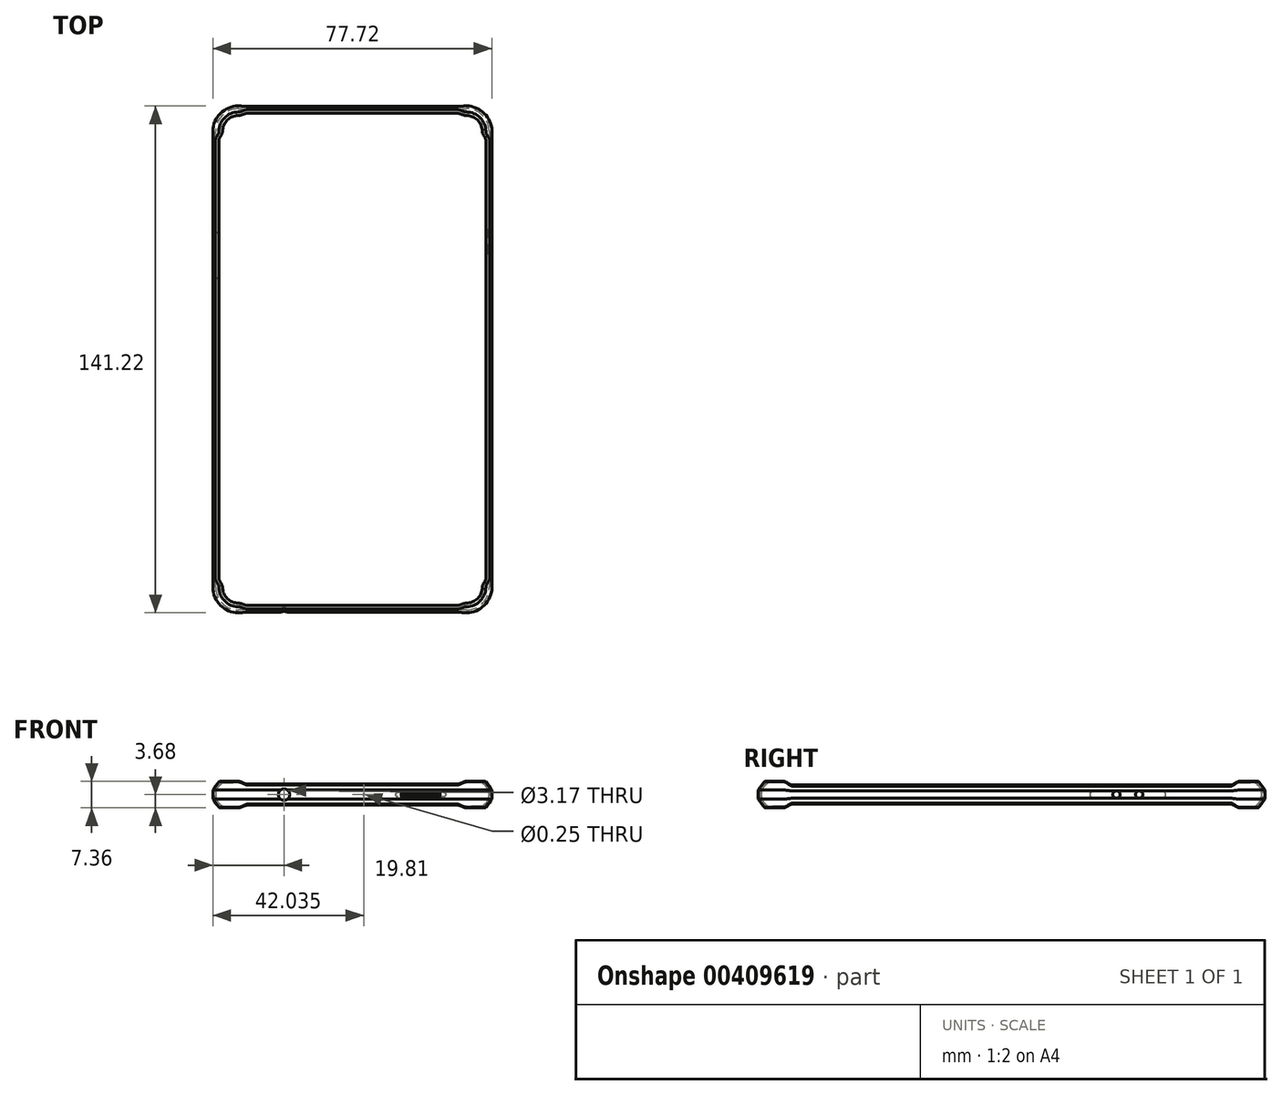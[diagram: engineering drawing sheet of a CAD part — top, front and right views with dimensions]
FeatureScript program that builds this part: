
annotation { "Feature Type Name" : "Feature", "Feature Type Description" : "" }
export const myFeature = defineFeature(function(context is Context, id is Id, definition is map)
    precondition{}
    {
        {
            var Q0;
            Q0=qCreatedBy(makeId("Top.planeOp"),FACE);
            var sketch = newSketch(context, id + "F0", { "sketchPlane" : qUnion([Q0])});
            skLineSegment(sketch, "E0", {"start": v(0, 0) * mm, "end": v(0, -63.5) * mm});
            skLineSegment(sketch, "E1", {"start": v(6.35, -69.85) * mm, "end": v(38.1, -69.85) * mm});
            skPoint(sketch, "E2.visualSharp", {"position": v(0, -69.85) * mm});
            skArc(sketch, "E2.filletArc", {"start": v(0, -63.5) * mm, "mid": v(1.86, -68) * mm, "end": v(6.35, -69.85) * mm});
            skSolve(sketch);
        }
        {
            var Q0;
            Q0=sQuery(id+"F0.wireOp",EDGE,"E1");
            var Q1;
            Q1=sQuery(id+"F0.wireOp",VERTEX,"E1.end");
            cPlane(context, id + "F1", {"entities" : qUnion([Q0, Q1]), "cplaneType" : CPlaneType.LINE_POINT, "offset" : 25.4 * mm, "width" : 152.4 * mm, "height" : 152.4 * mm});
        }
        {
            var Q0;
            Q0=qCreatedBy(id+"F1.planeOp",FACE);
            var sketch = newSketch(context, id + "F2", { "sketchPlane" : qUnion([Q0])});
            skLineSegment(sketch, "E3", {"start": v(-69.68, 0) * mm, "end": v(-65.87, 0) * mm});
            skArc(sketch, "E4", {"start": v(-68.57, 2.7) * mm, "mid": v(-69.68, 0) * mm, "end": v(-68.57, -2.7) * mm});
            skLineSegment(sketch, "E5", {"start": v(-68.57, 2.7) * mm, "end": v(-68.62, 2.75) * mm});
            skLineSegment(sketch, "E6", {"start": v(-68.62, 2.75) * mm, "end": v(-68.57, 2.7) * mm});
            skLineSegment(sketch, "E7", {"start": v(-69.68, 0) * mm, "end": v(-70.44, 0) * mm});
            skLineSegment(sketch, "E8", {"start": v(-70.44, 0) * mm, "end": v(-70.44, 1.27) * mm});
            skLineSegment(sketch, "E9", {"start": v(-70.44, 0) * mm, "end": v(-70.44, -1.27) * mm});
            skLineSegment(sketch, "E10", {"start": v(-68.57, -2.7) * mm, "end": v(-68.62, -2.75) * mm});
            skPoint(sketch, "E11.visualSharp", {"position": v(-69.1, 3.23) * mm});
            skArc(sketch, "E11.filletArc", {"start": v(-68.62, 2.75) * mm, "mid": v(-69.12, 2.93) * mm, "end": v(-69.58, 2.67) * mm});
            skPoint(sketch, "E12.visualSharp", {"position": v(-69.1, -3.23) * mm});
            skArc(sketch, "E12.filletArc", {"start": v(-69.58, -2.67) * mm, "mid": v(-69.12, -2.93) * mm, "end": v(-68.62, -2.75) * mm});
            skLineSegment(sketch, "E13", {"start": v(-70.44, 1.27) * mm, "end": v(-69.58, 2.67) * mm});
            skLineSegment(sketch, "E14", {"start": v(-70.44, -1.27) * mm, "end": v(-69.58, -2.67) * mm});
            skSolve(sketch);
        }
        {
            var Q0;
            Q0 = qSketchRegion(id + "F2", true);
            extrude(context, id + "F3", {"entities" : qUnion([Q0]), "oppositeDirection" : true, "depth" : 29.2 * mm});
        }
        {
            var Q0;
            Q0=qCreatedBy(makeId("Front.planeOp"),FACE);
            var sketch = newSketch(context, id + "F4", { "sketchPlane" : qUnion([Q0])});
            skLineSegment(sketch, "E15", {"start": v(0, 0) * mm, "end": v(3.81, 0) * mm});
            skArc(sketch, "E16", {"start": v(0.9, 2.45) * mm, "mid": v(0, 0) * mm, "end": v(0.9, -2.45) * mm});
            skLineSegment(sketch, "E17", {"start": v(0.9, 2.45) * mm, "end": v(0.83, 2.5) * mm});
            skLineSegment(sketch, "E18", {"start": v(0, 0) * mm, "end": v(-0.76, 0) * mm});
            skLineSegment(sketch, "E19", {"start": v(0.9, -2.45) * mm, "end": v(0.83, -2.5) * mm});
            skLineSegment(sketch, "E20", {"start": v(-0.76, 0) * mm, "end": v(-0.76, 1.02) * mm});
            skLineSegment(sketch, "E21", {"start": v(-0.76, 0) * mm, "end": v(-0.76, -1.02) * mm});
            skPoint(sketch, "E22.visualSharp", {"position": v(0.3, 2.94) * mm});
            skArc(sketch, "E22.filletArc", {"start": v(0.83, 2.5) * mm, "mid": v(0.32, 2.64) * mm, "end": v(-0.12, 2.34) * mm});
            skPoint(sketch, "E23.visualSharp", {"position": v(0.3, -2.94) * mm});
            skArc(sketch, "E23.filletArc", {"start": v(-0.12, -2.34) * mm, "mid": v(0.32, -2.64) * mm, "end": v(0.83, -2.5) * mm});
            skLineSegment(sketch, "E24", {"start": v(-0.76, 1.02) * mm, "end": v(-0.12, 2.34) * mm});
            skLineSegment(sketch, "E25", {"start": v(-0.76, -1.02) * mm, "end": v(-0.12, -2.34) * mm});
            skSolve(sketch);
        }
        {
            var Q0;
            Q0 = qSketchRegion(id + "F4", true);
            extrude(context, id + "F5", {"entities" : qUnion([Q0]), "depth" : 60.96 * mm});
        }
        {
            var Q0;
            Q0=sQuery(id+"F0.wireOp",EDGE,"E0");
            var Q1;
            Q1=sQuery(id+"F0.wireOp",VERTEX,"E2.filletArc.start");
            cPlane(context, id + "F6", {"entities" : qUnion([Q0, Q1]), "cplaneType" : CPlaneType.LINE_POINT, "offset" : 25.4 * mm, "width" : 152.4 * mm, "height" : 152.4 * mm});
        }
        {
            var Q0;
            Q0=qCreatedBy(id+"F6.planeOp",FACE);
            var sketch = newSketch(context, id + "F7", { "sketchPlane" : qUnion([Q0])});
            skLineSegment(sketch, "E26", {"start": v(0, 0) * mm, "end": v(3.8, 0) * mm});
            skArc(sketch, "E27", {"start": v(1.9, 3.3) * mm, "mid": v(0, 0) * mm, "end": v(1.9, -3.3) * mm});
            skLineSegment(sketch, "E28", {"start": v(1.9, 3.3) * mm, "end": v(1.87, 3.36) * mm});
            skLineSegment(sketch, "E29", {"start": v(1.9, -3.3) * mm, "end": v(1.87, -3.36) * mm});
            skLineSegment(sketch, "E30", {"start": v(0, 0) * mm, "end": v(-0.76, 0) * mm});
            skLineSegment(sketch, "E31", {"start": v(-0.76, 0) * mm, "end": v(-0.76, 1.27) * mm});
            skLineSegment(sketch, "E32", {"start": v(-0.76, 0) * mm, "end": v(-0.76, -1.27) * mm});
            skPoint(sketch, "E33.visualSharp", {"position": v(1.52, 3.96) * mm});
            skArc(sketch, "E33.filletArc", {"start": v(1.87, 3.36) * mm, "mid": v(1.43, 3.67) * mm, "end": v(0.92, 3.54) * mm});
            skPoint(sketch, "E34.visualSharp", {"position": v(1.52, -3.96) * mm});
            skArc(sketch, "E34.filletArc", {"start": v(0.92, -3.54) * mm, "mid": v(1.43, -3.67) * mm, "end": v(1.87, -3.36) * mm});
            skLineSegment(sketch, "E35", {"start": v(-0.76, 1.27) * mm, "end": v(0.92, 3.54) * mm});
            skLineSegment(sketch, "E36", {"start": v(-0.76, -1.27) * mm, "end": v(0.92, -3.54) * mm});
            skSolve(sketch);
        }
        {
            var Q0;
            {var subQ1=sQuery(id+"F7.wireOp",EDGE,"E29");Q0=makeQuery(id+"F7.imprint","IMPRINT",FACE,{"disambiguationData":[TD([[makeQuery(id+"F7.imprint","IMPRINT",EDGE,{"derivedFrom":subQ1}),-1.0]])]});}
            var Q1;
            {var subQ1=sQuery(id+"F7.wireOp",EDGE,"E28");Q1=makeQuery(id+"F7.imprint","IMPRINT",FACE,{"disambiguationData":[TD([[makeQuery(id+"F7.imprint","IMPRINT",EDGE,{"derivedFrom":subQ1}),1.0]])]});}
            var Q2;
            Q2=sQuery(id+"F0.wireOp",EDGE,"E2.filletArc");
            sweep(context, id + "F8", {"profiles" : qUnion([Q0, Q1]), "path" : qUnion([Q2])});
        }
        {
            var Q0;
            Q0=makeQuery(id+"F8.opSweep","CAP_FACE",FACE,{"disambiguationData":[OSD([sQuery(id+"F0.wireOp",VERTEX,"E2.filletArc.end"),sQuery(id+"F7.wireOp",EDGE,"E27"),sQuery(id+"F7.wireOp",EDGE,"E28"),sQuery(id+"F7.wireOp",EDGE,"E29"),sQuery(id+"F7.wireOp",EDGE,"E31"),sQuery(id+"F7.wireOp",EDGE,"E32"),sQuery(id+"F7.wireOp",EDGE,"E33.filletArc"),sQuery(id+"F7.wireOp",EDGE,"E34.filletArc"),sQuery(id+"F7.wireOp",EDGE,"E35"),sQuery(id+"F7.wireOp",EDGE,"E36")])],"isStart":false});
            var Q1;
            Q1=makeQuery(id+"F3.opExtrude","CAP_FACE",FACE,{"disambiguationData":[OSD([sQuery(id+"F2.wireOp",EDGE,"E4"),sQuery(id+"F2.wireOp",EDGE,"E6"),sQuery(id+"F2.wireOp",EDGE,"E8"),sQuery(id+"F2.wireOp",EDGE,"E9"),sQuery(id+"F2.wireOp",EDGE,"E10"),sQuery(id+"F2.wireOp",EDGE,"E11.filletArc"),sQuery(id+"F2.wireOp",EDGE,"E12.filletArc"),sQuery(id+"F2.wireOp",EDGE,"E13"),sQuery(id+"F2.wireOp",EDGE,"E14")])],"isStart":false});
            loft(context, id + "F9", {"operationType" : NewBodyOperationType.ADD, "startCondition" : LoftEndDerivativeType.NORMAL_TO_PROFILE, "startMagnitude" : 1, "endCondition" : LoftEndDerivativeType.NORMAL_TO_PROFILE, "endMagnitude" : 1, "sheetProfilesArray" : [{ "sheetProfileEntities" : qUnion([Q0]) }, { "sheetProfileEntities" : qUnion([Q1]) }]});
        }
        {
            var Q0;
            Q0=makeQuery(id+"F5.opExtrude","CAP_FACE",FACE,{"disambiguationData":[OSD([sQuery(id+"F4.wireOp",EDGE,"E16"),sQuery(id+"F4.wireOp",EDGE,"E17"),sQuery(id+"F4.wireOp",EDGE,"E19"),sQuery(id+"F4.wireOp",EDGE,"E20"),sQuery(id+"F4.wireOp",EDGE,"E21"),sQuery(id+"F4.wireOp",EDGE,"E22.filletArc"),sQuery(id+"F4.wireOp",EDGE,"E23.filletArc"),sQuery(id+"F4.wireOp",EDGE,"E24"),sQuery(id+"F4.wireOp",EDGE,"E25")])],"isStart":false});
            var Q1;
            Q1=makeQuery(id+"F8.opSweep","CAP_FACE",FACE,{"disambiguationData":[OSD([sQuery(id+"F0.wireOp",VERTEX,"E2.filletArc.start"),sQuery(id+"F7.wireOp",EDGE,"E27"),sQuery(id+"F7.wireOp",EDGE,"E28"),sQuery(id+"F7.wireOp",EDGE,"E29"),sQuery(id+"F7.wireOp",EDGE,"E31"),sQuery(id+"F7.wireOp",EDGE,"E32"),sQuery(id+"F7.wireOp",EDGE,"E33.filletArc"),sQuery(id+"F7.wireOp",EDGE,"E34.filletArc"),sQuery(id+"F7.wireOp",EDGE,"E35"),sQuery(id+"F7.wireOp",EDGE,"E36")])],"isStart":true});
            loft(context, id + "F10", {"operationType" : NewBodyOperationType.ADD, "startCondition" : LoftEndDerivativeType.NORMAL_TO_PROFILE, "startMagnitude" : 1, "endCondition" : LoftEndDerivativeType.NORMAL_TO_PROFILE, "endMagnitude" : 1, "sheetProfilesArray" : [{ "sheetProfileEntities" : qUnion([Q0]) }, { "sheetProfileEntities" : qUnion([Q1]) }]});
        }
        {
            var Q0;
            Q0=makeQuery(id+"F3.opExtrude","SWEPT_BODY",BODY,{"disambiguationData":[OSD([sQuery(id+"F2.wireOp",EDGE,"E4"),sQuery(id+"F2.wireOp",EDGE,"E6"),sQuery(id+"F2.wireOp",EDGE,"E8"),sQuery(id+"F2.wireOp",EDGE,"E9"),sQuery(id+"F2.wireOp",EDGE,"E10"),sQuery(id+"F2.wireOp",EDGE,"E11.filletArc"),sQuery(id+"F2.wireOp",EDGE,"E12.filletArc"),sQuery(id+"F2.wireOp",EDGE,"E13"),sQuery(id+"F2.wireOp",EDGE,"E14")])]});
            var Q1;
            Q1=makeQuery(id+"F3.opExtrude","CAP_FACE",FACE,{"disambiguationData":[OSD([sQuery(id+"F2.wireOp",EDGE,"E4"),sQuery(id+"F2.wireOp",EDGE,"E6"),sQuery(id+"F2.wireOp",EDGE,"E8"),sQuery(id+"F2.wireOp",EDGE,"E9"),sQuery(id+"F2.wireOp",EDGE,"E10"),sQuery(id+"F2.wireOp",EDGE,"E11.filletArc"),sQuery(id+"F2.wireOp",EDGE,"E12.filletArc"),sQuery(id+"F2.wireOp",EDGE,"E13"),sQuery(id+"F2.wireOp",EDGE,"E14")])],"isStart":true});
            mirror(context, id + "F11", {"operationType" : NewBodyOperationType.ADD, "entities" : qUnion([Q0]), "mirrorPlane" : qUnion([Q1])});
        }
        {
            var Q0;
            Q0=makeQuery(id+"F3.opExtrude","SWEPT_BODY",BODY,{"disambiguationData":[OSD([sQuery(id+"F2.wireOp",EDGE,"E4"),sQuery(id+"F2.wireOp",EDGE,"E6"),sQuery(id+"F2.wireOp",EDGE,"E8"),sQuery(id+"F2.wireOp",EDGE,"E9"),sQuery(id+"F2.wireOp",EDGE,"E10"),sQuery(id+"F2.wireOp",EDGE,"E11.filletArc"),sQuery(id+"F2.wireOp",EDGE,"E12.filletArc"),sQuery(id+"F2.wireOp",EDGE,"E13"),sQuery(id+"F2.wireOp",EDGE,"E14")])]});
            var Q1;
            Q1=makeQuery(id+"F11.opPattern","COPY",FACE,{"derivedFrom":makeQuery(id+"F5.opExtrude","CAP_FACE",FACE,{"disambiguationData":[OSD([sQuery(id+"F4.wireOp",EDGE,"E16"),sQuery(id+"F4.wireOp",EDGE,"E17"),sQuery(id+"F4.wireOp",EDGE,"E19"),sQuery(id+"F4.wireOp",EDGE,"E20"),sQuery(id+"F4.wireOp",EDGE,"E21"),sQuery(id+"F4.wireOp",EDGE,"E22.filletArc"),sQuery(id+"F4.wireOp",EDGE,"E23.filletArc"),sQuery(id+"F4.wireOp",EDGE,"E24"),sQuery(id+"F4.wireOp",EDGE,"E25")])],"isStart":true}),"instanceName":"1"});
            mirror(context, id + "F12", {"operationType" : NewBodyOperationType.ADD, "entities" : qUnion([Q0]), "mirrorPlane" : qUnion([Q1])});
        }
        {
            var Q0;
            {var subQ0=sQuery(id+"F4.wireOp",EDGE,"E21");var subQ1=sQuery(id+"F4.wireOp",EDGE,"E20");var subQ2=makeQuery(id+"F11.opPattern","COPY",FACE,{"derivedFrom":makeQuery(id+"F10.boolean.opBoolean","MERGE",FACE,{"derivedFrom":[makeQuery(id+"F5.opExtrude","SWEPT_FACE",FACE,{"disambiguationData":[OSD([subQ1,subQ0])]}),makeQuery(id+"F10.opLoft","SWEPT_FACE",FACE,{"disambiguationData":[OSD([sQuery(id+"F0.wireOp",VERTEX,"E2.filletArc.start"),sQuery(id+"F0.wireOp",EDGE,"E2.filletArc"),subQ1,subQ0,sQuery(id+"F4.wireOp",EDGE,"E24"),sQuery(id+"F4.wireOp",EDGE,"E25"),sQuery(id+"F7.wireOp",EDGE,"E31"),sQuery(id+"F7.wireOp",EDGE,"E32"),sQuery(id+"F7.wireOp",EDGE,"E35"),sQuery(id+"F7.wireOp",EDGE,"E36")])]})]}),"instanceName":"1"});Q0=makeQuery(id+"F12.boolean.opBoolean","MERGE",FACE,{"derivedFrom":[subQ2,makeQuery(id+"F12.opPattern","COPY",FACE,{"derivedFrom":subQ2,"instanceName":"1"})]});}
            var sketch = newSketch(context, id + "F13", { "sketchPlane" : qUnion([Q0])});
            skLineSegment(sketch, "E37", {"start": v(60.96, 1.02) * mm, "end": v(60.96, 0) * mm});
            skLineSegment(sketch, "E38", {"start": v(60.96, 0) * mm, "end": v(36.58, 0) * mm});
            skLineSegment(sketch, "E39", {"start": v(29.2, 0) * mm, "end": v(29.2, 0) * mm});
            skArc(sketch, "E40", {"start": v(35.56, -1.02) * mm, "mid": v(36.58, 0) * mm, "end": v(35.56, 1.02) * mm});
            skArc(sketch, "E41", {"start": v(29.2, 1.02) * mm, "mid": v(28.2, 0) * mm, "end": v(29.2, -1.02) * mm});
            skLineSegment(sketch, "E42.bottom", {"start": v(29.2, -1.02) * mm, "end": v(35.56, -1.02) * mm});
            skLineSegment(sketch, "E42.top", {"start": v(29.2, 1.02) * mm, "end": v(35.56, 1.02) * mm});
            skSolve(sketch);
        }
        {
            var Q0;
            Q0=makeQuery(id+"F13.imprint","IMPRINT",FACE,{"disambiguationData":[TD([[makeQuery(id+"F13.imprint","IMPRINT",EDGE,{"derivedFrom":sQuery(id+"F13.wireOp",EDGE,"E41")}),1.0]])]});
            extrude(context, id + "F14", {"entities" : qUnion([Q0]), "operationType" : NewBodyOperationType.REMOVE, "oppositeDirection" : true, "depth" : 6.35 * mm});
        }
        {
            var Q0;
            {var subQ0=sQuery(id+"F4.wireOp",EDGE,"E21");var subQ1=sQuery(id+"F4.wireOp",EDGE,"E20");var subQ2=makeQuery(id+"F10.boolean.opBoolean","MERGE",FACE,{"derivedFrom":[makeQuery(id+"F5.opExtrude","SWEPT_FACE",FACE,{"disambiguationData":[OSD([subQ1,subQ0])]}),makeQuery(id+"F10.opLoft","SWEPT_FACE",FACE,{"disambiguationData":[OSD([sQuery(id+"F0.wireOp",VERTEX,"E2.filletArc.start"),sQuery(id+"F0.wireOp",EDGE,"E2.filletArc"),subQ1,subQ0,sQuery(id+"F4.wireOp",EDGE,"E24"),sQuery(id+"F4.wireOp",EDGE,"E25"),sQuery(id+"F7.wireOp",EDGE,"E31"),sQuery(id+"F7.wireOp",EDGE,"E32"),sQuery(id+"F7.wireOp",EDGE,"E35"),sQuery(id+"F7.wireOp",EDGE,"E36")])]})]});Q0=makeQuery(id+"F12.boolean.opBoolean","MERGE",FACE,{"derivedFrom":[subQ2,makeQuery(id+"F12.opPattern","COPY",FACE,{"derivedFrom":subQ2,"instanceName":"1"})]});}
            var sketch = newSketch(context, id + "F15", { "sketchPlane" : qUnion([Q0])});
            skArc(sketch, "E43", {"start": v(-41.9, 1.02) * mm, "mid": v(-42.93, 0) * mm, "end": v(-41.9, -1.02) * mm});
            skArc(sketch, "E44", {"start": v(-35.56, -1.02) * mm, "mid": v(-34.54, 0) * mm, "end": v(-35.56, 1.02) * mm});
            skArc(sketch, "E45", {"start": v(-29.2, 1.02) * mm, "mid": v(-30.23, 0) * mm, "end": v(-29.2, -1.02) * mm});
            skArc(sketch, "E46", {"start": v(-22.86, -1.02) * mm, "mid": v(-21.84, 0) * mm, "end": v(-22.86, 1.02) * mm});
            skLineSegment(sketch, "E47.bottom", {"start": v(-41.9, 1.02) * mm, "end": v(-35.56, 1.02) * mm});
            skLineSegment(sketch, "E47.top", {"start": v(-41.9, -1.02) * mm, "end": v(-35.56, -1.02) * mm});
            skLineSegment(sketch, "E48.trimOffspring", {"start": v(-29.2, 1.02) * mm, "end": v(-22.86, 1.02) * mm});
            skLineSegment(sketch, "E49.trimOffspring", {"start": v(-29.2, -1.02) * mm, "end": v(-22.86, -1.02) * mm});
            skSolve(sketch);
        }
        {
            var Q0;
            Q0 = qSketchRegion(id + "F15", true);
            extrude(context, id + "F16", {"entities" : qUnion([Q0]), "operationType" : NewBodyOperationType.REMOVE, "oppositeDirection" : true, "depth" : 6.35 * mm});
        }
        {
            var Q0;
            {var subQ0=makeQuery(id+"F3.opExtrude","SWEPT_FACE",FACE,{"disambiguationData":[OSD([sQuery(id+"F2.wireOp",EDGE,"E8"),sQuery(id+"F2.wireOp",EDGE,"E9")])]});Q0=makeQuery(id+"F11.boolean.opBoolean","MERGE",FACE,{"derivedFrom":[subQ0,makeQuery(id+"F11.opPattern","COPY",FACE,{"derivedFrom":subQ0,"instanceName":"1"})]});}
            var sketch = newSketch(context, id + "F17", { "sketchPlane" : qUnion([Q0])});
            skLineSegment(sketch, "E50", {"start": v(38.1, 1.27) * mm, "end": v(38.1, 0) * mm});
            skPoint(sketch, "E50.endSnap0", {"position": v(38.1, -1.27) * mm});
            skLineSegment(sketch, "E51", {"start": v(38.1, 0) * mm, "end": v(19.05, 0) * mm});
            skLineSegment(sketch, "E52", {"start": v(38.1, 0) * mm, "end": v(57.15, 0) * mm});
            skCircle(sketch, "E53", {"center": v(41.28, 0) * mm, "radius": 0.13 * mm});
            skCircle(sketch, "E54", {"center": v(19.05, 0) * mm, "radius": 1.59 * mm});
            skSolve(sketch);
        }
        {
            var Q0;
            Q0 = qSketchRegion(id + "F17", true);
            var Q1;
            {var subQ0=sQuery(id+"F17.wireOp",EDGE,"E54");var subQ1=makeQuery(id+"F17.imprint","INTERSECT",VERTEX,{"derivedFrom":[sQuery(id+"F17.wireOp",EDGE,"E51"),subQ0]});Q1=makeQuery(id+"F17.imprint","IMPRINT",FACE,{"disambiguationData":[TD([[makeQuery(id+"F17.imprint","IMPRINT",EDGE,{"disambiguationData":[TD([[subQ1,-1.0]])],"derivedFrom":subQ0}),1.0]])]});}
            extrude(context, id + "F18", {"entities" : qUnion([Q0, Q1]), "operationType" : NewBodyOperationType.REMOVE, "oppositeDirection" : true, "depth" : 6.35 * mm});
        }
        {
            var Q0;
            {var subQ6=sQuery(id+"F2.wireOp",EDGE,"E9");var subQ11=sQuery(id+"F2.wireOp",EDGE,"E8");var subQ12=makeQuery(id+"F3.opExtrude","SWEPT_FACE",FACE,{"disambiguationData":[OSD([subQ11,subQ6])]});Q0=makeQuery(id+"F18.boolean.opBoolean","SPLIT",FACE,{"disambiguationData":[TD([makeQuery(id+"F18.opExtrude","SWEPT_FACE",FACE,{"disambiguationData":[OSD([sQuery(id+"F17.wireOp",EDGE,"E53")])]})])],"derivedFrom":makeQuery(id+"F11.boolean.opBoolean","MERGE",FACE,{"derivedFrom":[subQ12,makeQuery(id+"F11.opPattern","COPY",FACE,{"derivedFrom":subQ12,"instanceName":"1"})]})});}
            var sketch = newSketch(context, id + "F19", { "sketchPlane" : qUnion([Q0])});
            skArc(sketch, "E55", {"start": v(53, 1.27) * mm, "mid": v(51.74, 0) * mm, "end": v(53, -1.27) * mm});
            skArc(sketch, "E56", {"start": v(61.3, -1.27) * mm, "mid": v(62.56, 0) * mm, "end": v(61.3, 1.27) * mm});
            skLineSegment(sketch, "E57", {"start": v(53, -1.27) * mm, "end": v(61.3, -1.27) * mm});
            skLineSegment(sketch, "E58", {"start": v(53, 1.27) * mm, "end": v(61.3, 1.27) * mm});
            skArc(sketch, "E59.0", {"start": v(53, 0.89) * mm, "mid": v(52.12, 0) * mm, "end": v(53, -0.89) * mm});
            skLineSegment(sketch, "E59.1", {"start": v(53, 0.89) * mm, "end": v(61.3, 0.89) * mm});
            skArc(sketch, "E59.2", {"start": v(61.3, -0.89) * mm, "mid": v(62.18, 0) * mm, "end": v(61.3, 0.89) * mm});
            skLineSegment(sketch, "E59.3", {"start": v(53, -0.89) * mm, "end": v(61.3, -0.89) * mm});
            skArc(sketch, "E60.0", {"start": v(53, 0.25) * mm, "mid": v(52.76, 0) * mm, "end": v(53, -0.25) * mm});
            skLineSegment(sketch, "E60.1", {"start": v(53, 0.25) * mm, "end": v(61.3, 0.25) * mm});
            skArc(sketch, "E60.2", {"start": v(61.3, -0.25) * mm, "mid": v(61.54, 0) * mm, "end": v(61.3, 0.25) * mm});
            skLineSegment(sketch, "E60.3", {"start": v(53, -0.25) * mm, "end": v(61.3, -0.25) * mm});
            skSolve(sketch);
        }
        {
            var Q0;
            Q0 = qSketchRegion(id + "F19", true);
            var Q1;
            Q1=makeQuery(id+"F19.imprint","IMPRINT",FACE,{"disambiguationData":[TD([[makeQuery(id+"F19.imprint","IMPRINT",EDGE,{"derivedFrom":sQuery(id+"F19.wireOp",EDGE,"E60.0")}),1.0]])]});
            extrude(context, id + "F20", {"entities" : qUnion([Q0, Q1]), "operationType" : NewBodyOperationType.REMOVE, "oppositeDirection" : true, "depth" : 0.38 * mm});
        }
        {
            var Q0;
            {var subQ0=makeQuery(id+"F3.opExtrude","SWEPT_FACE",FACE,{"disambiguationData":[OSD([sQuery(id+"F2.wireOp",EDGE,"E8"),sQuery(id+"F2.wireOp",EDGE,"E9")])]});Q0=makeQuery(id+"F12.opPattern","COPY",FACE,{"derivedFrom":makeQuery(id+"F11.boolean.opBoolean","MERGE",FACE,{"derivedFrom":[subQ0,makeQuery(id+"F11.opPattern","COPY",FACE,{"derivedFrom":subQ0,"instanceName":"1"})]}),"instanceName":"1"});}
            var sketch = newSketch(context, id + "F21", { "sketchPlane" : qUnion([Q0])});
            skLineSegment(sketch, "E61", {"start": v(-38.1, 1.27) * mm, "end": v(-38.1, 0) * mm});
            skPoint(sketch, "E61.endSnap0", {"position": v(-38.1, 1.27) * mm});
            skLineSegment(sketch, "E62", {"start": v(-38.1, 0) * mm, "end": v(-50.17, 0) * mm});
            skArc(sketch, "E63", {"start": v(-50.8, -0.64) * mm, "mid": v(-50.17, 0) * mm, "end": v(-50.8, 0.64) * mm});
            skArc(sketch, "E64", {"start": v(-63.5, 0.64) * mm, "mid": v(-64.14, 0) * mm, "end": v(-63.5, -0.64) * mm});
            skLineSegment(sketch, "E65", {"start": v(-63.5, -0.64) * mm, "end": v(-50.8, -0.64) * mm});
            skLineSegment(sketch, "E66", {"start": v(-50.8, 0.64) * mm, "end": v(-63.5, 0.64) * mm});
            skSolve(sketch);
        }
        {
            var Q0;
            Q0=makeQuery(id+"F21.imprint","IMPRINT",FACE,{"disambiguationData":[TD([[makeQuery(id+"F21.imprint","IMPRINT",EDGE,{"derivedFrom":sQuery(id+"F21.wireOp",EDGE,"E64")}),1.0]])]});
            extrude(context, id + "F22", {"entities" : qUnion([Q0]), "operationType" : NewBodyOperationType.REMOVE, "oppositeDirection" : true, "depth" : 6.35 * mm});
        }
    });
